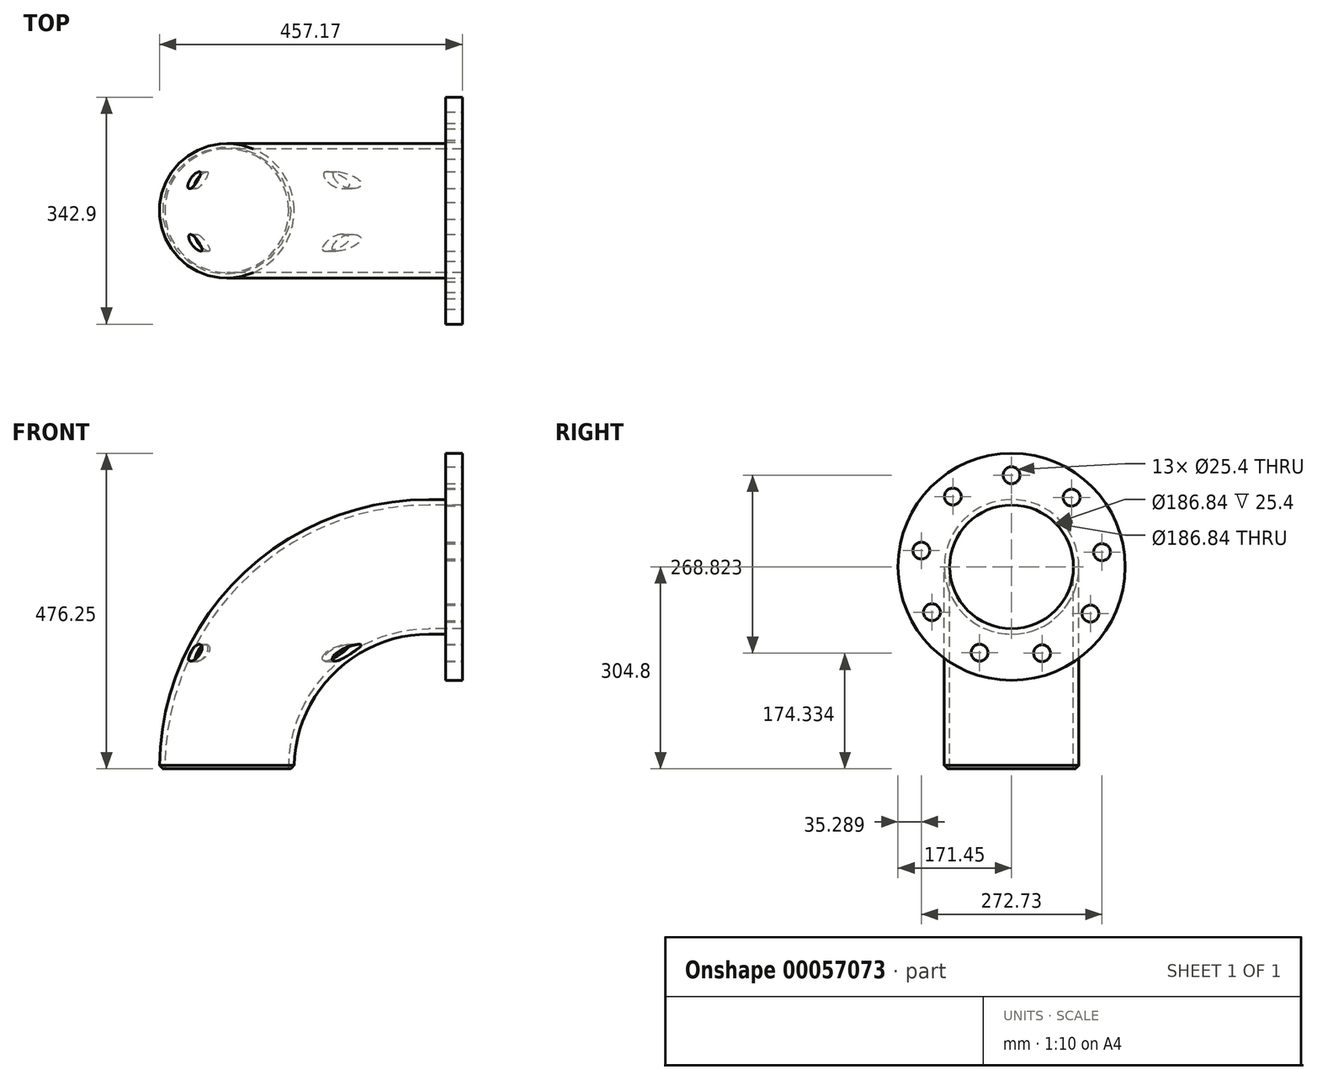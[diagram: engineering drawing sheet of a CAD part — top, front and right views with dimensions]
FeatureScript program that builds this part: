
annotation { "Feature Type Name" : "Feature", "Feature Type Description" : "" }
export const myFeature = defineFeature(function(context is Context, id is Id, definition is map)
    precondition{}
    {
        {
            var Q0;
            Q0=qCreatedBy(makeId("Top.planeOp"),FACE);
            var sketch = newSketch(context, id + "F0", { "sketchPlane" : qUnion([Q0])});
            skCircle(sketch, "E0", {"center": v(0, 0) * mm, "radius": 101.6 * mm});
            skCircle(sketch, "E1", {"center": v(0, 0) * mm, "radius": 93.42 * mm});
            skSolve(sketch);
        }
        {
            var Q0;
            Q0=qCreatedBy(makeId("Front.planeOp"),FACE);
            var sketch = newSketch(context, id + "F1", { "sketchPlane" : qUnion([Q0])});
            skArc(sketch, "E2", {"start": v(0, 0) * mm, "mid": v(89.27, 215.53) * mm, "end": v(304.8, 304.8) * mm});
            skSolve(sketch);
        }
        {
            var Q0;
            Q0=makeQuery(id+"F0.imprint","IMPRINT",FACE,{"disambiguationData":[TD([[makeQuery(id+"F0.imprint","IMPRINT",EDGE,{"derivedFrom":sQuery(id+"F0.wireOp",EDGE,"E0")}),1.0]])]});
            var Q1;
            Q1=sQuery(id+"F1.wireOp",EDGE,"E2");
            sweep(context, id + "F2", {"profiles" : qUnion([Q0]), "path" : qUnion([Q1])});
        }
        {
            var Q0;
            Q0=makeQuery(id+"F2.opSweep","CAP_FACE",FACE,{"disambiguationData":[OSD([sQuery(id+"F0.wireOp",EDGE,"E0"),sQuery(id+"F0.wireOp",EDGE,"E1"),sQuery(id+"F1.wireOp",VERTEX,"E2.end")])],"isStart":false});
            extrude(context, id + "F3", {"entities" : qUnion([Q0]), "operationType" : NewBodyOperationType.ADD, "depth" : 25.4 * mm});
        }
        {
            var Q0;
            Q0=makeQuery(id+"F3.opExtrude","CAP_FACE",FACE,{"disambiguationData":[OSD([sQuery(id+"F0.wireOp",EDGE,"E0"),sQuery(id+"F0.wireOp",EDGE,"E1"),sQuery(id+"F1.wireOp",VERTEX,"E2.end")])],"isStart":false});
            var sketch = newSketch(context, id + "F4", { "sketchPlane" : qUnion([Q0])});
            skCircle(sketch, "E3", {"center": v(0, 304.8) * mm, "radius": 171.45 * mm});
            skCircle(sketch, "E4", {"center": v(0, 304.8) * mm, "radius": 93.42 * mm});
            skSolve(sketch);
        }
        {
            var Q0;
            Q0 = qSketchRegion(id + "F4", true);
            extrude(context, id + "F5", {"entities" : qUnion([Q0]), "depth" : 25.4 * mm});
        }
        {
            var Q0;
            Q0=makeQuery(id+"F2.opSweep","CAP_EDGE",EDGE,{"disambiguationData":[OSD([sQuery(id+"F0.wireOp",EDGE,"E0"),sQuery(id+"F1.wireOp",VERTEX,"E2.start")])],"isStart":true});
            chamfer(context, id + "F6", {"entities" : qUnion([Q0]), "width" : 5.08 * mm, "tangentPropagation" : true});
        }
        {
            var Q0;
            Q0=makeQuery(id+"F5.opExtrude","CAP_FACE",FACE,{"disambiguationData":[OSD([sQuery(id+"F4.wireOp",EDGE,"E3"),sQuery(id+"F4.wireOp",EDGE,"E4")])],"isStart":false});
            var sketch = newSketch(context, id + "F7", { "sketchPlane" : qUnion([Q0])});
            skArc(sketch, "E5", {"start": v(2.41, 443.14) * mm, "mid": v(1.2, 443.15) * mm, "end": v(0, 443.16) * mm});
            skPoint(sketch, "E6.orphan", {"position": v(0, 443.16) * mm});
            skPoint(sketch, "E7.start.orphan", {"position": v(138.36, 304.8) * mm});
            skCircle(sketch, "E8", {"center": v(0, 443.16) * mm, "radius": 12.7 * mm});
            skLineSegment(sketch, "E9.anchor1", {"start": v(0, 304.8) * mm, "end": v(0, 443.16) * mm, "construction": true});
            skLineSegment(sketch, "E9.anchor2", {"start": v(0, 304.8) * mm, "end": v(0, 443.16) * mm, "construction": true});
            skCircle(sketch, "E10.1.0", {"center": v(-88.73, 410.96) * mm, "radius": 12.7 * mm});
            skCircle(sketch, "E10.2.0", {"center": v(-136.16, 329.35) * mm, "radius": 12.7 * mm});
            skCircle(sketch, "E10.3.0", {"center": v(-120.22, 236.32) * mm, "radius": 12.7 * mm});
            skCircle(sketch, "E10.4.0", {"center": v(-48.33, 175.16) * mm, "radius": 12.7 * mm});
            skCircle(sketch, "E10.5.0", {"center": v(46.06, 174.33) * mm, "radius": 12.7 * mm});
            skCircle(sketch, "E10.6.0", {"center": v(119, 234.23) * mm, "radius": 12.7 * mm});
            skCircle(sketch, "E10.7.0", {"center": v(136.57, 326.97) * mm, "radius": 12.7 * mm});
            skCircle(sketch, "E10.8.0", {"center": v(90.57, 409.4) * mm, "radius": 12.7 * mm});
            skLineSegment(sketch, "E10.anchor2", {"start": v(0, 304.8) * mm, "end": v(2.41, 443.14) * mm, "construction": true});
            skSolve(sketch);
        }
        {
            var Q0;
            Q0=makeQuery(id+"F7.imprint","IMPRINT",FACE,{"disambiguationData":[TD([[makeQuery(id+"F7.imprint","IMPRINT",EDGE,{"derivedFrom":sQuery(id+"F7.wireOp",EDGE,"E10.1.0")}),1.0]])]});
            var Q1;
            Q1=makeQuery(id+"F7.imprint","IMPRINT",FACE,{"disambiguationData":[TD([[makeQuery(id+"F7.imprint","IMPRINT",EDGE,{"derivedFrom":sQuery(id+"F7.wireOp",EDGE,"E8")}),1.0]])]});
            var Q2;
            Q2=makeQuery(id+"F7.imprint","IMPRINT",FACE,{"disambiguationData":[TD([[makeQuery(id+"F7.imprint","IMPRINT",EDGE,{"derivedFrom":sQuery(id+"F7.wireOp",EDGE,"E10.8.0")}),1.0]])]});
            var Q3;
            Q3=makeQuery(id+"F7.imprint","IMPRINT",FACE,{"disambiguationData":[TD([[makeQuery(id+"F7.imprint","IMPRINT",EDGE,{"derivedFrom":sQuery(id+"F7.wireOp",EDGE,"E10.7.0")}),1.0]])]});
            var Q4;
            Q4=makeQuery(id+"F7.imprint","IMPRINT",FACE,{"disambiguationData":[TD([[makeQuery(id+"F7.imprint","IMPRINT",EDGE,{"derivedFrom":sQuery(id+"F7.wireOp",EDGE,"E10.6.0")}),1.0]])]});
            var Q5;
            Q5=makeQuery(id+"F7.imprint","IMPRINT",FACE,{"disambiguationData":[TD([[makeQuery(id+"F7.imprint","IMPRINT",EDGE,{"derivedFrom":sQuery(id+"F7.wireOp",EDGE,"E10.5.0")}),1.0]])]});
            var Q6;
            Q6=makeQuery(id+"F7.imprint","IMPRINT",FACE,{"disambiguationData":[TD([[makeQuery(id+"F7.imprint","IMPRINT",EDGE,{"derivedFrom":sQuery(id+"F7.wireOp",EDGE,"E10.4.0")}),1.0]])]});
            var Q7;
            Q7=makeQuery(id+"F7.imprint","IMPRINT",FACE,{"disambiguationData":[TD([[makeQuery(id+"F7.imprint","IMPRINT",EDGE,{"derivedFrom":sQuery(id+"F7.wireOp",EDGE,"E10.3.0")}),1.0]])]});
            var Q8;
            Q8=makeQuery(id+"F7.imprint","IMPRINT",FACE,{"disambiguationData":[TD([[makeQuery(id+"F7.imprint","IMPRINT",EDGE,{"derivedFrom":sQuery(id+"F7.wireOp",EDGE,"E10.2.0")}),1.0]])]});
            extrude(context, id + "F8", {"entities" : qUnion([Q0, Q1, Q2, Q3, Q4, Q5, Q6, Q7, Q8]), "operationType" : NewBodyOperationType.REMOVE, "endBound" : BoundingType.THROUGH_ALL, "oppositeDirection" : true, "depth" : 25.4 * mm});
        }
        {
            var Q0;
            Q0=makeQuery(id+"F5.opExtrude","SWEPT_BODY",BODY,{"disambiguationData":[OSD([sQuery(id+"F4.wireOp",EDGE,"E3"),sQuery(id+"F4.wireOp",EDGE,"E4")])]});
            transform(context, id + "F9", {"entities" : qUnion([Q0]), "transformType" : TransformType.TRANSLATION_3D, "dx" : 0 * mm, "dy" : 0 * mm, "dz" : 0 * mm, "makeCopy" : true});
        }
        {
            var Q0;
            Q0=makeQuery(id+"F9.opPattern","COPY",BODY,{"derivedFrom":makeQuery(id+"F5.opExtrude","SWEPT_BODY",BODY,{"disambiguationData":[OSD([sQuery(id+"F4.wireOp",EDGE,"E3"),sQuery(id+"F4.wireOp",EDGE,"E4")])]}),"instanceName":"1"});
            deleteBodies(context, id + "F10", {"entities" : qUnion([Q0])});
        }
    });
